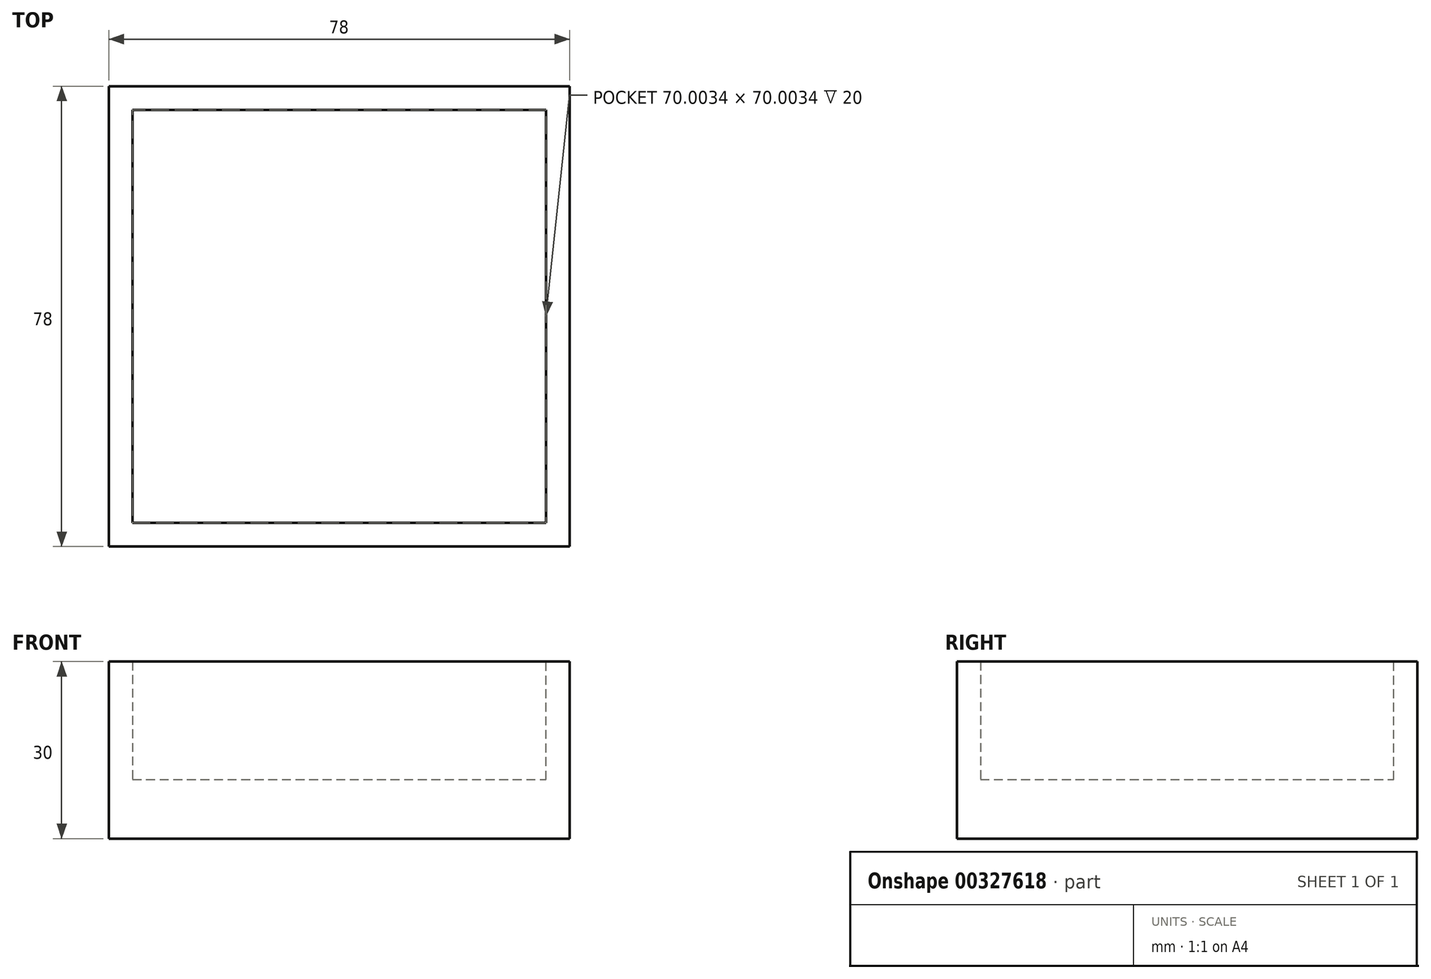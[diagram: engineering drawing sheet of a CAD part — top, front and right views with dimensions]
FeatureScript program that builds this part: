
annotation { "Feature Type Name" : "Feature", "Feature Type Description" : "" }
export const myFeature = defineFeature(function(context is Context, id is Id, definition is map)
    precondition{}
    {
        {
            var Q0;
            Q0=qCreatedBy(makeId("Top.planeOp"),FACE);
            var sketch = newSketch(context, id + "F0", { "sketchPlane" : qUnion([Q0])});
            skLineSegment(sketch, "E0.bottom", {"start": v(0, 0) * mm, "end": v(78, 0) * mm});
            skLineSegment(sketch, "E0.top", {"start": v(0, -78) * mm, "end": v(78, -78) * mm});
            skLineSegment(sketch, "E0.left", {"start": v(0, 0) * mm, "end": v(0, -78) * mm});
            skLineSegment(sketch, "E0.right", {"start": v(78, 0) * mm, "end": v(78, -78) * mm});
            skLineSegment(sketch, "E1.bottom", {"start": v(4, -74) * mm, "end": v(74, -74) * mm});
            skLineSegment(sketch, "E1.top", {"start": v(4, -4) * mm, "end": v(74, -4) * mm});
            skLineSegment(sketch, "E1.left", {"start": v(4, -74) * mm, "end": v(4, -4) * mm});
            skLineSegment(sketch, "E1.right", {"start": v(74, -74) * mm, "end": v(74, -4) * mm});
            skSolve(sketch);
        }
        {
            var Q0;
            Q0 = qSketchRegion(id + "F0", true);
            extrude(context, id + "F1", {"entities" : qUnion([Q0]), "depth" : 30 * mm});
        }
        {
            var Q0;
            Q0=qCreatedBy(makeId("Top.planeOp"),FACE);
            var sketch = newSketch(context, id + "F2", { "sketchPlane" : qUnion([Q0])});
            skLineSegment(sketch, "E2.bottom", {"start": v(4, -74) * mm, "end": v(74, -74) * mm});
            skLineSegment(sketch, "E2.top", {"start": v(4, -4) * mm, "end": v(74, -4) * mm});
            skLineSegment(sketch, "E2.left", {"start": v(4, -74) * mm, "end": v(4, -4) * mm});
            skLineSegment(sketch, "E2.right", {"start": v(74, -74) * mm, "end": v(74, -4) * mm});
            skSolve(sketch);
        }
        {
            var Q0;
            Q0 = qSketchRegion(id + "F2", true);
            extrude(context, id + "F3", {"entities" : qUnion([Q0]), "operationType" : NewBodyOperationType.ADD, "depth" : 10 * mm});
        }
    });
